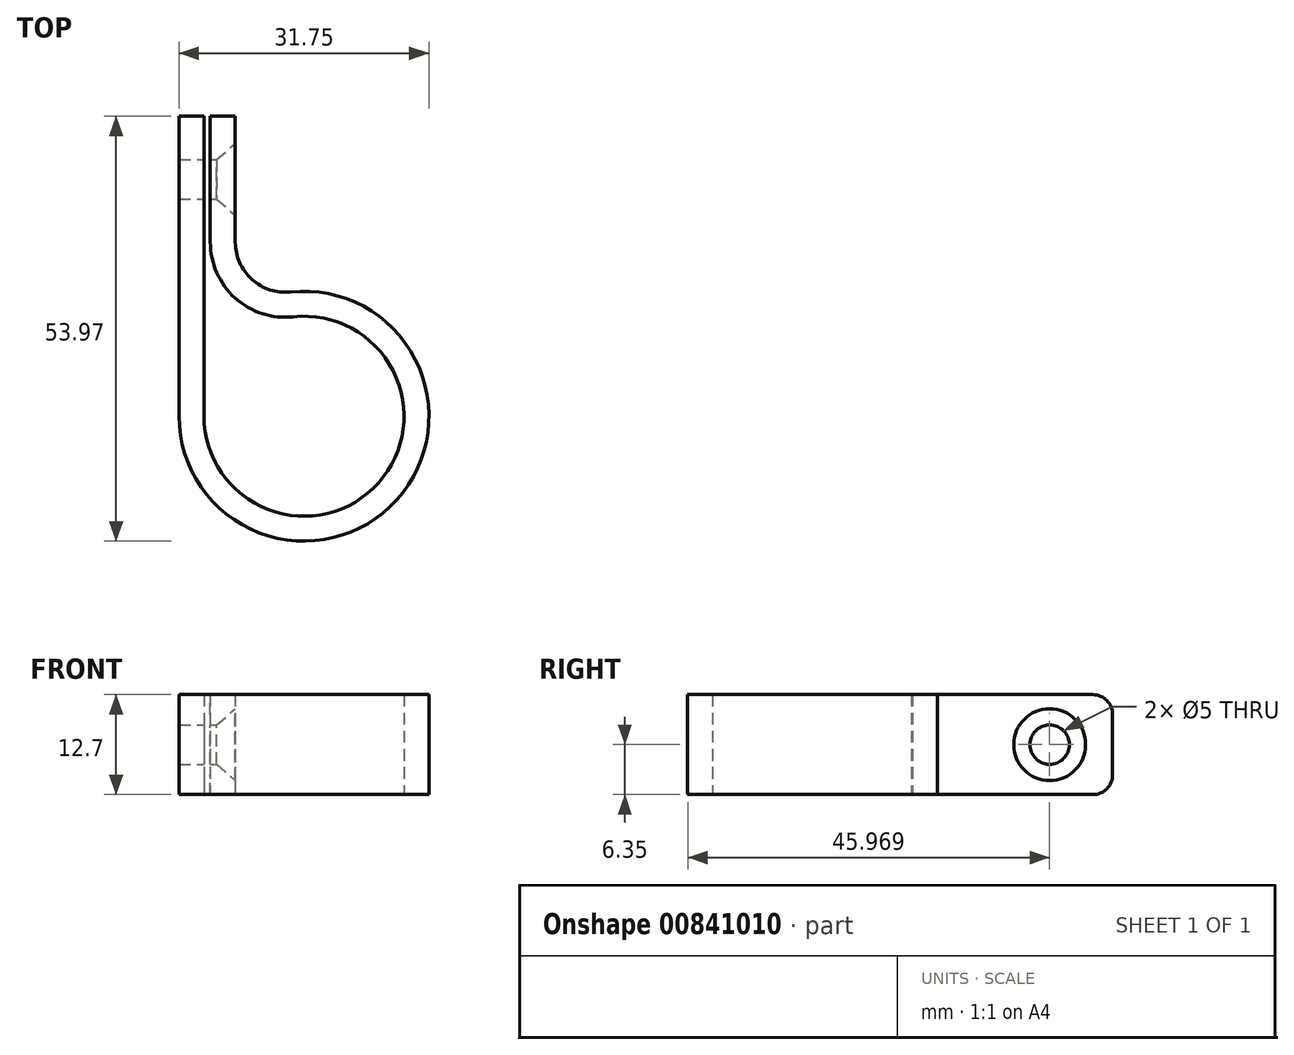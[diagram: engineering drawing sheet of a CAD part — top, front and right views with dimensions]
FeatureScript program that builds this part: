
annotation { "Feature Type Name" : "Feature", "Feature Type Description" : "" }
export const myFeature = defineFeature(function(context is Context, id is Id, definition is map)
    precondition{}
    {
        {
            var Q0;
            Q0=qCreatedBy(makeId("Top.planeOp"),FACE);
            var sketch = newSketch(context, id + "F0", { "sketchPlane" : qUnion([Q0])});
            skArc(sketch, "E0", {"start": v(-12.7, 0) * mm, "mid": v(11.66, -5.02) * mm, "end": v(-8.72, 9.23) * mm});
            skArc(sketch, "E1", {"start": v(-15.88, 0) * mm, "mid": v(11.8, -10.6) * mm, "end": v(-1.7, 15.78) * mm});
            skLineSegment(sketch, "E2", {"start": v(-15.88, 0) * mm, "end": v(-15.88, 38.1) * mm});
            skLineSegment(sketch, "E3", {"start": v(-12.7, 0) * mm, "end": v(-12.7, 38.1) * mm});
            skLineSegment(sketch, "E4", {"start": v(-12.7, 38.1) * mm, "end": v(-15.88, 38.1) * mm});
            skLineSegment(sketch, "E5", {"start": v(-12.7, 38.1) * mm, "end": v(-11.9, 38.1) * mm, "construction": true});
            skLineSegment(sketch, "E6", {"start": v(-11.9, 38.1) * mm, "end": v(-11.9, 12.4) * mm});
            skLineSegment(sketch, "E7", {"start": v(-11.9, 0) * mm, "end": v(-8.72, 0) * mm, "construction": true});
            skLineSegment(sketch, "E8", {"start": v(-8.72, 22.1) * mm, "end": v(-8.72, 38.1) * mm});
            skLineSegment(sketch, "E9", {"start": v(-8.72, 38.1) * mm, "end": v(-11.9, 38.1) * mm});
            skLineSegment(sketch, "E10", {"start": v(-8.72, 9.23) * mm, "end": v(-8.72, 9.23) * mm});
            skPoint(sketch, "E11.visualSharp", {"position": v(-8.72, 13.26) * mm});
            skArc(sketch, "E11.filletArc", {"start": v(-8.72, 22.1) * mm, "mid": v(-6.62, 17.37) * mm, "end": v(-1.7, 15.78) * mm});
            skPoint(sketch, "E12.visualSharp", {"position": v(-11.9, 9.23) * mm});
            skArc(sketch, "E12.filletArc", {"start": v(-11.9, 12.4) * mm, "mid": v(-10.97, 10.16) * mm, "end": v(-8.72, 9.23) * mm});
            skArc(sketch, "E13.0", {"start": v(-11.9, 22.1) * mm, "mid": v(-8.74, 15.01) * mm, "end": v(-1.36, 12.63) * mm});
            skSolve(sketch);
        }
        {
            var Q0;
            Q0=makeQuery(id+"F0.imprint","IMPRINT",FACE,{"disambiguationData":[TD([[makeQuery(id+"F0.imprint","IMPRINT",EDGE,{"derivedFrom":sQuery(id+"F0.wireOp",EDGE,"E1")}),1.0]])]});
            extrude(context, id + "F1", {"entities" : qUnion([Q0]), "endBound" : BoundingType.SYMMETRIC, "depth" : 12.7 * mm, "offsetDistance" : 25.4 * mm});
        }
        {
            var Q0;
            Q0=makeQuery(id+"F1.opExtrude","SWEPT_FACE",FACE,{"disambiguationData":[OSD([sQuery(id+"F0.wireOp",EDGE,"E8")])]});
            var sketch = newSketch(context, id + "F2", { "sketchPlane" : qUnion([Q0])});
            skLineSegment(sketch, "E14", {"start": v(38.1, 6.35) * mm, "end": v(22.1, -6.35) * mm, "construction": true});
            skPoint(sketch, "E15", {"position": v(30.1, 0) * mm});
            skSolve(sketch);
        }
        {
            var Q0;
            Q0=sQuery(id+"F2.wireOp",VERTEX,"E15");
            var Q1;
            Q1=makeQuery(id+"F1.opExtrude","SWEPT_BODY",BODY,{"disambiguationData":[OSD([sQuery(id+"F0.wireOp",EDGE,"E0"),sQuery(id+"F0.wireOp",EDGE,"E1"),sQuery(id+"F0.wireOp",EDGE,"E2"),sQuery(id+"F0.wireOp",EDGE,"E3"),sQuery(id+"F0.wireOp",EDGE,"E4"),sQuery(id+"F0.wireOp",EDGE,"E6"),sQuery(id+"F0.wireOp",EDGE,"E8"),sQuery(id+"F0.wireOp",EDGE,"E9"),sQuery(id+"F0.wireOp",EDGE,"E11.filletArc"),sQuery(id+"F0.wireOp",EDGE,"E12.filletArc")])]});
            hole(context, id + "F3", {"style" : HoleStyle.C_SINK, "endStyle" : HoleEndStyle.THROUGH, "holeDiameter" : 5 * mm, "cSinkDiameter" : 9.12 * mm, "cSinkAngle" : 82 * degree, "majorDiameter" : 6.35 * mm, "isTappedThrough" : true, "tappedDepth" : 12.7 * mm, "tapClearance" : 3, "locations" : qUnion([Q0]), "scope" : qUnion([Q1])});
        }
        {
            var Q0;
            Q0=makeQuery(id+"F1.opExtrude","CAP_EDGE",EDGE,{"disambiguationData":[OSD([sQuery(id+"F0.wireOp",EDGE,"E4")])],"isStart":false});
            var Q1;
            Q1=makeQuery(id+"F1.opExtrude","CAP_EDGE",EDGE,{"disambiguationData":[OSD([sQuery(id+"F0.wireOp",EDGE,"E9")])],"isStart":true});
            var Q2;
            Q2=makeQuery(id+"F1.opExtrude","CAP_EDGE",EDGE,{"disambiguationData":[OSD([sQuery(id+"F0.wireOp",EDGE,"E4")])],"isStart":true});
            var Q3;
            Q3=makeQuery(id+"F1.opExtrude","CAP_EDGE",EDGE,{"disambiguationData":[OSD([sQuery(id+"F0.wireOp",EDGE,"E9")])],"isStart":false});
            fillet(context, id + "F4", {"entities" : qUnion([Q0, Q1, Q2, Q3]), "radius" : 2.54 * mm, "tangentPropagation" : true, "allowEdgeOverflow" : false});
        }
    });
